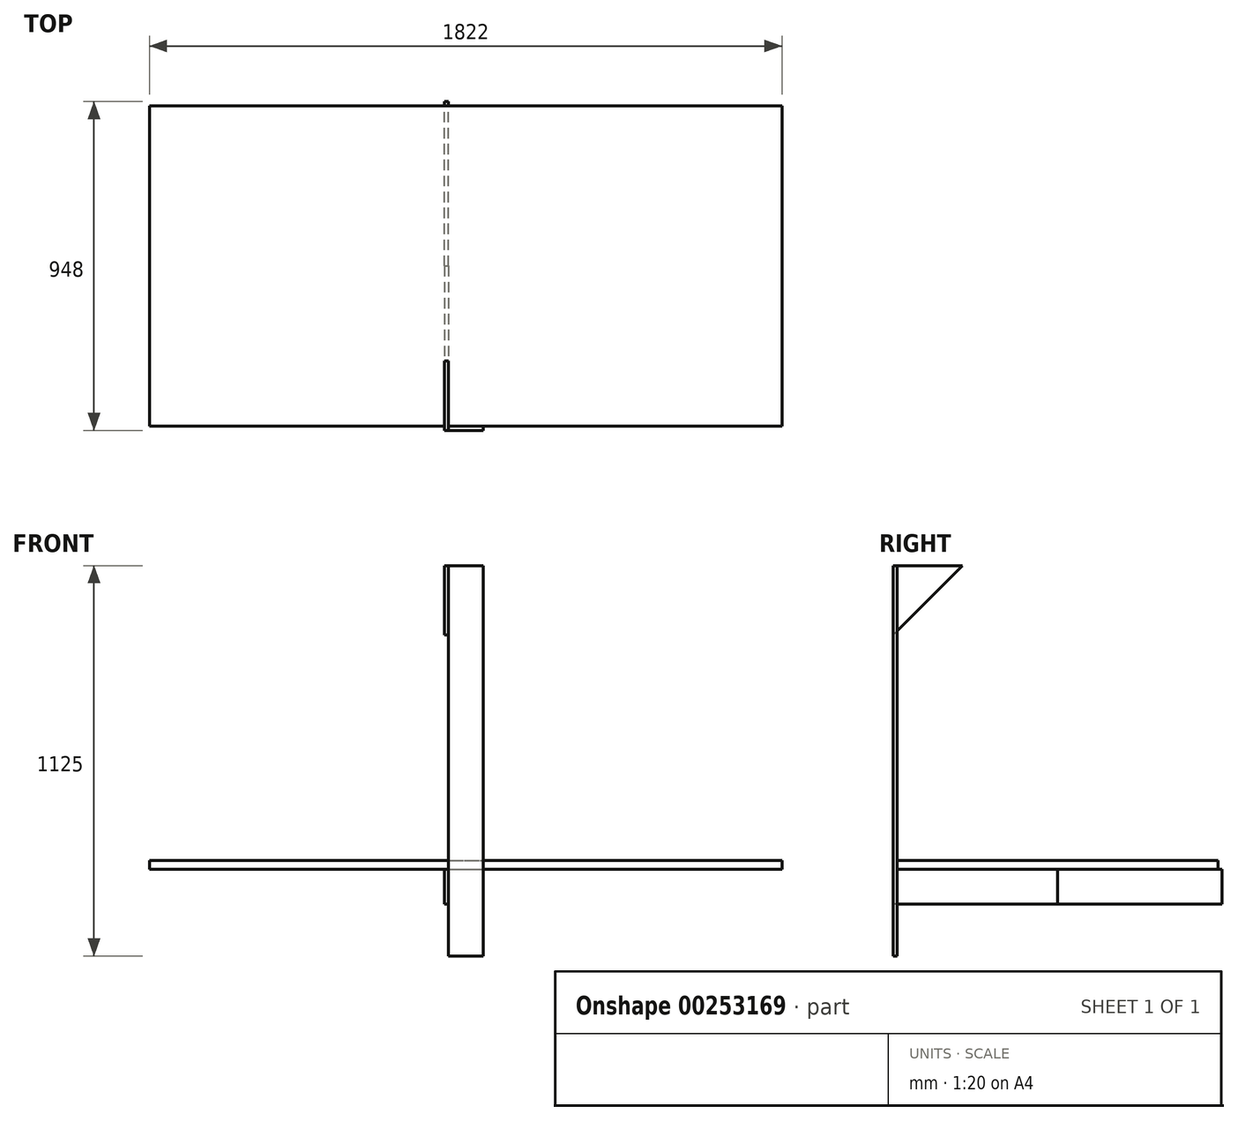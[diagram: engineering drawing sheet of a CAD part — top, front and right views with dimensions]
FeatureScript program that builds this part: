
annotation { "Feature Type Name" : "Feature", "Feature Type Description" : "" }
export const myFeature = defineFeature(function(context is Context, id is Id, definition is map)
    precondition{}
    {
        {
            var Q0;
            Q0=qCreatedBy(makeId("Top.planeOp"),FACE);
            var sketch = newSketch(context, id + "F0", { "sketchPlane" : qUnion([Q0])});
            skLineSegment(sketch, "E0.bottom", {"start": v(-911, 462) * mm, "end": v(911, 462) * mm});
            skLineSegment(sketch, "E0.top", {"start": v(-911, -462) * mm, "end": v(911, -462) * mm});
            skLineSegment(sketch, "E0.left", {"start": v(-911, 462) * mm, "end": v(-911, -462) * mm});
            skLineSegment(sketch, "E0.right", {"start": v(911, 462) * mm, "end": v(911, -462) * mm});
            skPoint(sketch, "E1", {"position": v(0, -462) * mm});
            skSolve(sketch);
        }
        {
            var Q0;
            Q0 = qSketchRegion(id + "F0", true);
            extrude(context, id + "F1", {"entities" : qUnion([Q0]), "depth" : 25 * mm});
        }
        {
            var Q0;
            Q0=makeQuery(id+"F1.opExtrude","SWEPT_FACE",FACE,{"disambiguationData":[OSD([sQuery(id+"F0.wireOp",EDGE,"E0.top")])]});
            var sketch = newSketch(context, id + "F2", { "sketchPlane" : qUnion([Q0])});
            skLineSegment(sketch, "E2.bottom", {"start": v(-50, 875) * mm, "end": v(50, 875) * mm});
            skLineSegment(sketch, "E2.top", {"start": v(-50, -250) * mm, "end": v(50, -250) * mm});
            skLineSegment(sketch, "E2.left", {"start": v(-50, 875) * mm, "end": v(-50, -250) * mm});
            skLineSegment(sketch, "E2.right", {"start": v(50, 875) * mm, "end": v(50, -250) * mm});
            skLineSegment(sketch, "E3", {"start": v(0, 875) * mm, "end": v(0, -250) * mm, "construction": true});
            skSolve(sketch);
        }
        {
            var Q0;
            Q0 = qSketchRegion(id + "F2", true);
            extrude(context, id + "F3", {"entities" : qUnion([Q0]), "depth" : 12 * mm});
        }
        {
            var Q0;
            Q0=makeQuery(id+"F3.opExtrude","SWEPT_FACE",FACE,{"disambiguationData":[OSD([sQuery(id+"F2.wireOp",EDGE,"E2.left")])]});
            var sketch = newSketch(context, id + "F4", { "sketchPlane" : qUnion([Q0])});
            skLineSegment(sketch, "E4.bottom", {"start": v(0, 0) * mm, "end": v(474, 0) * mm});
            skLineSegment(sketch, "E4.top", {"start": v(0, -100) * mm, "end": v(474, -100) * mm});
            skLineSegment(sketch, "E4.left", {"start": v(0, 0) * mm, "end": v(0, -100) * mm});
            skLineSegment(sketch, "E4.right", {"start": v(474, 0) * mm, "end": v(474, -100) * mm});
            skSolve(sketch);
        }
        {
            var Q0;
            Q0 = qSketchRegion(id + "F4", true);
            extrude(context, id + "F5", {"entities" : qUnion([Q0]), "depth" : 12 * mm});
        }
        {
            var Q0;
            Q0=makeQuery(id+"F5.opExtrude","SWEPT_BODY",BODY,{"disambiguationData":[OSD([sQuery(id+"F4.wireOp",EDGE,"E4.bottom"),sQuery(id+"F4.wireOp",EDGE,"E4.top"),sQuery(id+"F4.wireOp",EDGE,"E4.left"),sQuery(id+"F4.wireOp",EDGE,"E4.right")])]});
            var Q1;
            Q1=makeQuery(id+"F5.opExtrude","SWEPT_FACE",FACE,{"disambiguationData":[OSD([sQuery(id+"F4.wireOp",EDGE,"E4.left")])]});
            mirror(context, id + "F6", {"entities" : qUnion([Q0]), "mirrorPlane" : qUnion([Q1])});
        }
        {
            var Q0;
            Q0=makeQuery(id+"F3.opExtrude","SWEPT_FACE",FACE,{"disambiguationData":[OSD([sQuery(id+"F2.wireOp",EDGE,"E2.left")])]});
            var sketch = newSketch(context, id + "F7", { "sketchPlane" : qUnion([Q0])});
            skLineSegment(sketch, "E5", {"start": v(274, 875) * mm, "end": v(474, 675) * mm});
            skLineSegment(sketch, "E6", {"start": v(474, 675) * mm, "end": v(474, 875) * mm});
            skLineSegment(sketch, "E7", {"start": v(474, 875) * mm, "end": v(274, 875) * mm});
            skSolve(sketch);
        }
        {
            var Q0;
            Q0 = qSketchRegion(id + "F7", true);
            extrude(context, id + "F8", {"entities" : qUnion([Q0]), "depth" : 12 * mm});
        }
    });
